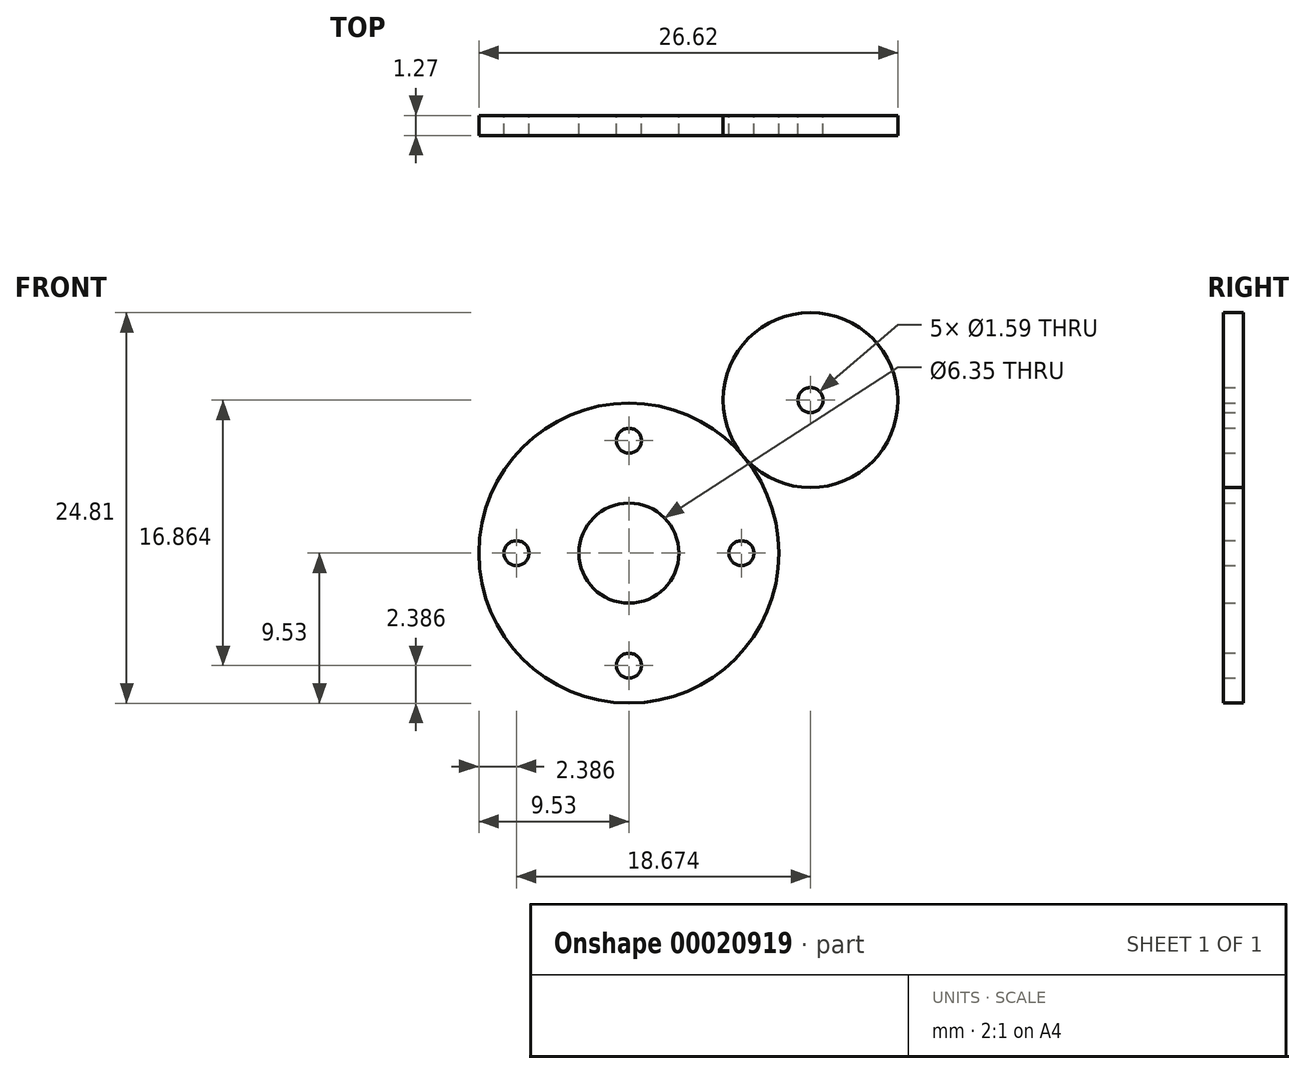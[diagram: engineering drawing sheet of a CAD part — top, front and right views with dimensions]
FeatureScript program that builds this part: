
annotation { "Feature Type Name" : "Feature", "Feature Type Description" : "" }
export const myFeature = defineFeature(function(context is Context, id is Id, definition is map)
    precondition{}
    {
        {
            var Q0;
            Q0=qCreatedBy(makeId("Front.planeOp"),FACE);
            var sketch = newSketch(context, id + "F0", { "sketchPlane" : qUnion([Q0])});
            skCircle(sketch, "E0", {"center": v(0, 0) * mm, "radius": 0.8 * mm});
            skCircle(sketch, "E1", {"center": v(0, 0) * mm, "radius": 7.94 * mm});
            skCircle(sketch, "E2", {"center": v(7.14, 0) * mm, "radius": 0.8 * mm});
            skCircle(sketch, "E3", {"center": v(-7.14, 0) * mm, "radius": 0.8 * mm});
            skCircle(sketch, "E4", {"center": v(0, 7.14) * mm, "radius": 0.8 * mm});
            skCircle(sketch, "E5", {"center": v(0, -7.14) * mm, "radius": 0.8 * mm});
            skCircle(sketch, "E6", {"center": v(0, 0) * mm, "radius": 3.18 * mm});
            skCircle(sketch, "E7", {"center": v(0, 0) * mm, "radius": 9.53 * mm});
            skCircle(sketch, "E8", {"center": v(11.53, 9.72) * mm, "radius": 0.8 * mm});
            skCircle(sketch, "E9", {"center": v(11.53, 9.72) * mm, "radius": 5.56 * mm});
            skLineSegment(sketch, "E10.trimOffspring", {"start": v(0, 0) * mm, "end": v(0, -0.8) * mm});
            skLineSegment(sketch, "E11.trimOffspring", {"start": v(0, -7.94) * mm, "end": v(0, -9.53) * mm});
            skSolve(sketch);
        }
        {
            var Q0;
            Q0=makeQuery(id+"F0.imprint","IMPRINT",FACE,{"disambiguationData":[TD([[makeQuery(id+"F0.imprint","IMPRINT",EDGE,{"derivedFrom":sQuery(id+"F0.wireOp",EDGE,"E7")}),1.0]])]});
            var Q1;
            {var subQ3=sQuery(id+"F0.wireOp",EDGE,"E2");Q1=makeQuery(id+"F0.imprint","IMPRINT",FACE,{"disambiguationData":[TD([[makeQuery(id+"F0.imprint","IMPRINT",EDGE,{"derivedFrom":subQ3}),-1.0]])]});}
            var Q2;
            Q2=makeQuery(id+"F0.imprint","IMPRINT",FACE,{"disambiguationData":[TD([[makeQuery(id+"F0.imprint","IMPRINT",EDGE,{"derivedFrom":sQuery(id+"F0.wireOp",EDGE,"E8")}),-1.0]])]});
            extrude(context, id + "F1", {"entities" : qUnion([Q0, Q1, Q2]), "depth" : 1.27 * mm});
        }
    });
